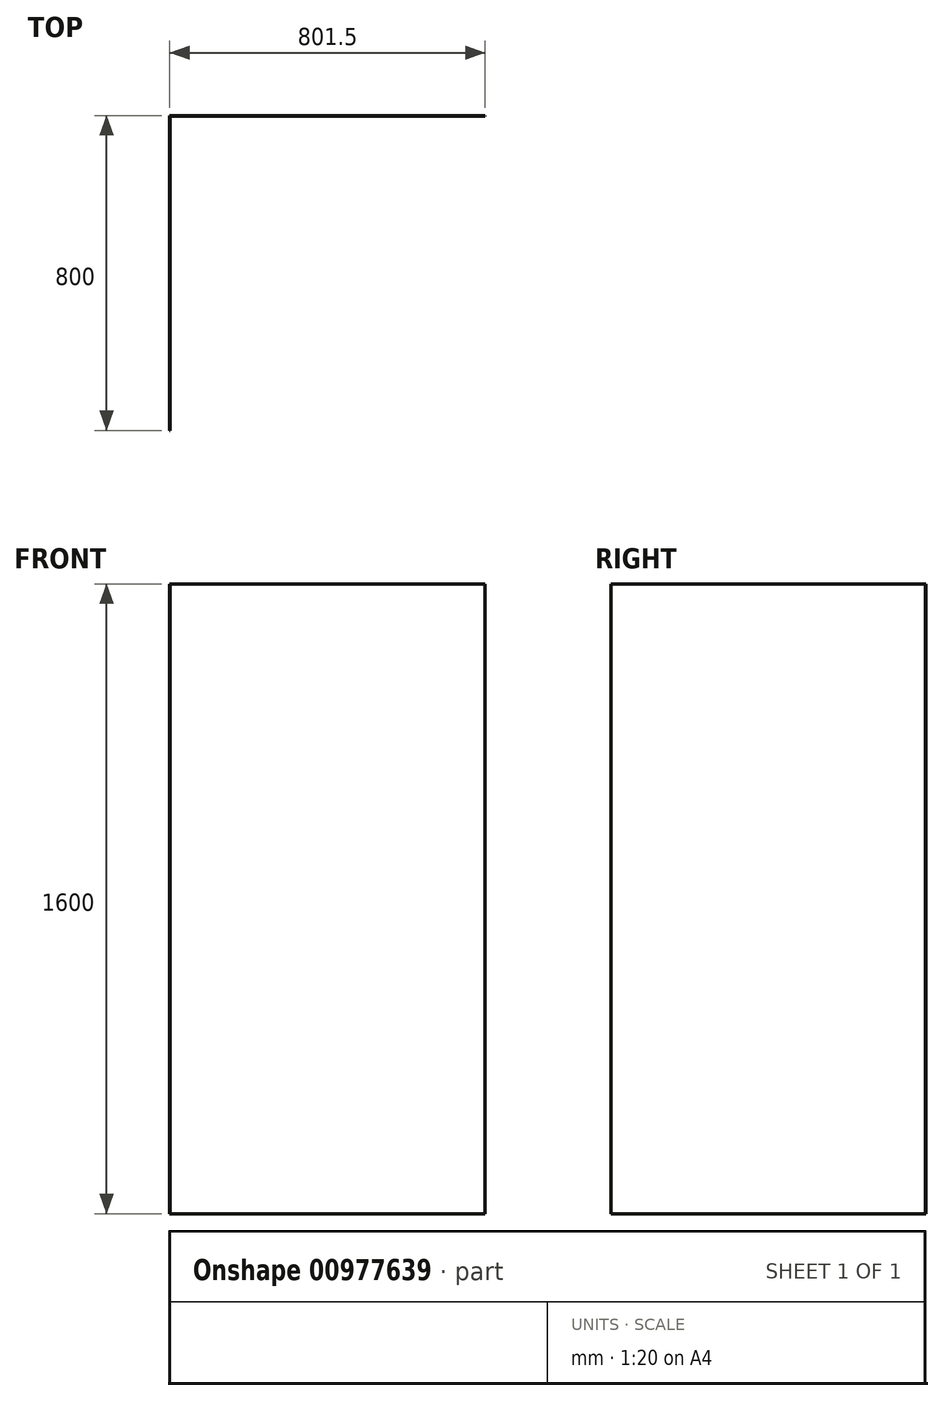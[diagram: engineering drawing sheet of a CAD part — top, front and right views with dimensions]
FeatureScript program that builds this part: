
annotation { "Feature Type Name" : "Feature", "Feature Type Description" : "" }
export const myFeature = defineFeature(function(context is Context, id is Id, definition is map)
    precondition{}
    {
        {
            var Q0;
            Q0=qCreatedBy(makeId("Front.planeOp"),FACE);
            var sketch = newSketch(context, id + "F0", { "sketchPlane" : qUnion([Q0])});
            skLineSegment(sketch, "E0.bottom", {"start": v(800, 1600) * mm, "end": v(0, 1600) * mm});
            skLineSegment(sketch, "E0.top", {"start": v(800, 0) * mm, "end": v(0, 0) * mm});
            skLineSegment(sketch, "E0.left", {"start": v(800, 1600) * mm, "end": v(800, 0) * mm});
            skLineSegment(sketch, "E0.right", {"start": v(0, 1600) * mm, "end": v(0, 0) * mm});
            skSolve(sketch);
        }
        {
            var Q0;
            Q0 = qSketchRegion(id + "F0", true);
            extrude(context, id + "F1", {"entities" : qUnion([Q0]), "depth" : 1.5 * mm, "offsetDistance" : 25 * mm});
        }
        {
            var Q0;
            Q0=qCreatedBy(makeId("Right.planeOp"),FACE);
            var sketch = newSketch(context, id + "F2", { "sketchPlane" : qUnion([Q0])});
            skLineSegment(sketch, "E1.bottom", {"start": v(-800, 0) * mm, "end": v(0, 0) * mm});
            skLineSegment(sketch, "E1.top", {"start": v(-800, 1600) * mm, "end": v(0, 1600) * mm});
            skLineSegment(sketch, "E1.left", {"start": v(-800, 0) * mm, "end": v(-800, 1600) * mm});
            skLineSegment(sketch, "E1.right", {"start": v(0, 0) * mm, "end": v(0, 1600) * mm});
            skSolve(sketch);
        }
        {
            var Q0;
            Q0 = qSketchRegion(id + "F2", true);
            extrude(context, id + "F3", {"entities" : qUnion([Q0]), "oppositeDirection" : true, "depth" : 1.5 * mm, "offsetDistance" : 25 * mm});
        }
    });
